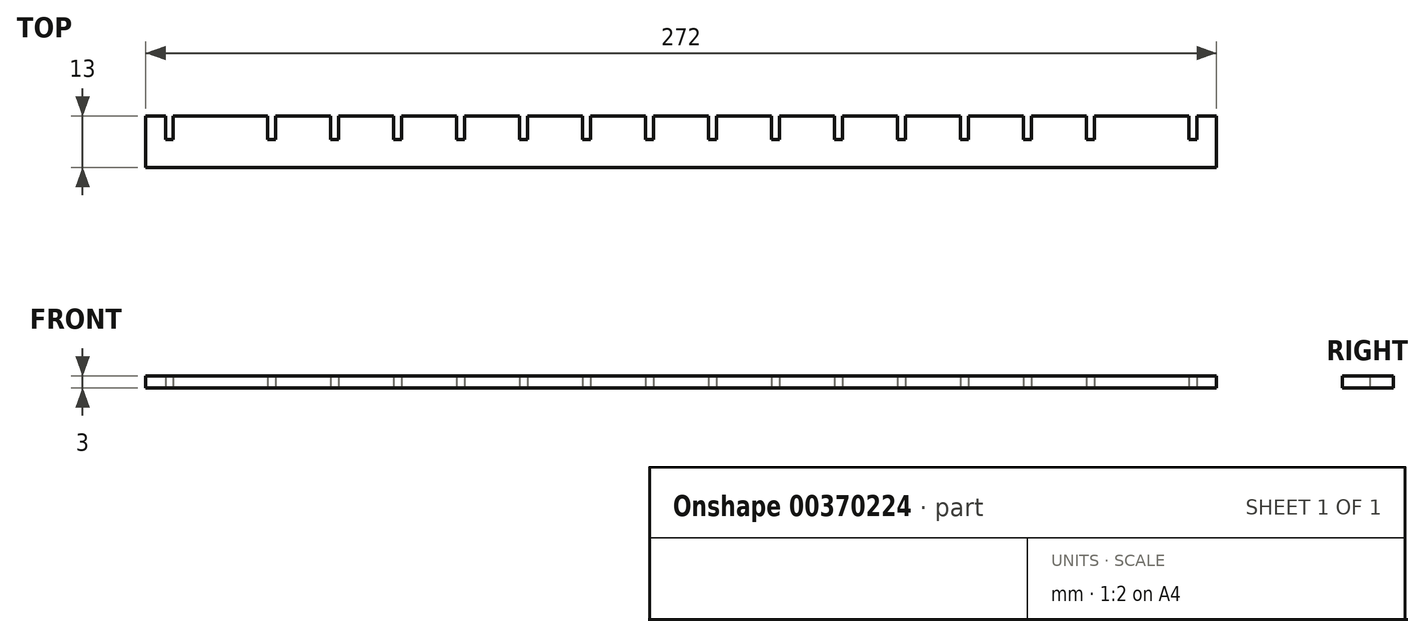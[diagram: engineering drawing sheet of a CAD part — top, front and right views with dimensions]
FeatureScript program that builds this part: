
annotation { "Feature Type Name" : "Feature", "Feature Type Description" : "" }
export const myFeature = defineFeature(function(context is Context, id is Id, definition is map)
    precondition{}
    {
        {
            var Q0;
            Q0=qCreatedBy(makeId("Top.planeOp"),FACE);
            var sketch = newSketch(context, id + "F0", { "sketchPlane" : qUnion([Q0])});
            skLineSegment(sketch, "E0.bottom", {"start": v(-189.77, 23.41) * mm, "end": v(82.23, 23.41) * mm});
            skLineSegment(sketch, "E0.top", {"start": v(-189.77, 10.41) * mm, "end": v(82.23, 10.41) * mm});
            skLineSegment(sketch, "E0.left", {"start": v(-189.77, 23.41) * mm, "end": v(-189.77, 10.41) * mm});
            skLineSegment(sketch, "E0.right", {"start": v(82.23, 23.41) * mm, "end": v(82.23, 10.41) * mm});
            skLineSegment(sketch, "E1.bottom", {"start": v(49.23, 23.41) * mm, "end": v(51.23, 23.41) * mm});
            skLineSegment(sketch, "E1.top", {"start": v(49.23, 17.41) * mm, "end": v(51.23, 17.41) * mm});
            skLineSegment(sketch, "E1.left", {"start": v(49.23, 23.41) * mm, "end": v(49.23, 17.41) * mm});
            skLineSegment(sketch, "E1.right", {"start": v(51.23, 23.41) * mm, "end": v(51.23, 17.41) * mm});
            skLineSegment(sketch, "E2.bottom", {"start": v(35.23, 23.41) * mm, "end": v(33.23, 23.41) * mm});
            skLineSegment(sketch, "E2.top", {"start": v(35.23, 17.41) * mm, "end": v(33.23, 17.41) * mm});
            skLineSegment(sketch, "E2.left", {"start": v(35.23, 23.41) * mm, "end": v(35.23, 17.41) * mm});
            skLineSegment(sketch, "E2.right", {"start": v(33.23, 23.41) * mm, "end": v(33.23, 17.41) * mm});
            skLineSegment(sketch, "E3.bottom", {"start": v(19.23, 23.41) * mm, "end": v(17.23, 23.41) * mm});
            skLineSegment(sketch, "E3.top", {"start": v(19.23, 17.41) * mm, "end": v(17.23, 17.41) * mm});
            skLineSegment(sketch, "E3.left", {"start": v(19.23, 23.41) * mm, "end": v(19.23, 17.41) * mm});
            skLineSegment(sketch, "E3.right", {"start": v(17.23, 23.41) * mm, "end": v(17.23, 17.41) * mm});
            skLineSegment(sketch, "E4.bottom", {"start": v(3.23, 23.41) * mm, "end": v(1.23, 23.41) * mm});
            skLineSegment(sketch, "E4.top", {"start": v(3.23, 17.41) * mm, "end": v(1.23, 17.41) * mm});
            skLineSegment(sketch, "E4.left", {"start": v(3.23, 23.41) * mm, "end": v(3.23, 17.41) * mm});
            skLineSegment(sketch, "E4.right", {"start": v(1.23, 23.41) * mm, "end": v(1.23, 17.41) * mm});
            skLineSegment(sketch, "E5.bottom", {"start": v(-12.77, 23.41) * mm, "end": v(-14.77, 23.41) * mm});
            skLineSegment(sketch, "E5.top", {"start": v(-12.77, 17.41) * mm, "end": v(-14.77, 17.41) * mm});
            skLineSegment(sketch, "E5.left", {"start": v(-12.77, 23.41) * mm, "end": v(-12.77, 17.41) * mm});
            skLineSegment(sketch, "E5.right", {"start": v(-14.77, 23.41) * mm, "end": v(-14.77, 17.41) * mm});
            skLineSegment(sketch, "E6.bottom", {"start": v(-28.77, 23.41) * mm, "end": v(-30.77, 23.41) * mm});
            skLineSegment(sketch, "E6.top", {"start": v(-28.77, 17.41) * mm, "end": v(-30.77, 17.41) * mm});
            skLineSegment(sketch, "E6.left", {"start": v(-28.77, 23.41) * mm, "end": v(-28.77, 17.41) * mm});
            skLineSegment(sketch, "E6.right", {"start": v(-30.77, 23.41) * mm, "end": v(-30.77, 17.41) * mm});
            skLineSegment(sketch, "E7.bottom", {"start": v(-108.77, 23.41) * mm, "end": v(-110.77, 23.41) * mm});
            skLineSegment(sketch, "E7.top", {"start": v(-108.77, 17.41) * mm, "end": v(-110.77, 17.41) * mm});
            skLineSegment(sketch, "E7.left", {"start": v(-108.77, 23.41) * mm, "end": v(-108.77, 17.41) * mm});
            skLineSegment(sketch, "E7.right", {"start": v(-110.77, 23.41) * mm, "end": v(-110.77, 17.41) * mm});
            skLineSegment(sketch, "E8.bottom", {"start": v(-44.77, 23.41) * mm, "end": v(-46.77, 23.41) * mm});
            skLineSegment(sketch, "E8.top", {"start": v(-44.77, 17.41) * mm, "end": v(-46.77, 17.41) * mm});
            skLineSegment(sketch, "E8.left", {"start": v(-44.77, 23.41) * mm, "end": v(-44.77, 17.41) * mm});
            skLineSegment(sketch, "E8.right", {"start": v(-46.77, 23.41) * mm, "end": v(-46.77, 17.41) * mm});
            skLineSegment(sketch, "E9.bottom", {"start": v(-62.77, 23.41) * mm, "end": v(-60.77, 23.41) * mm});
            skLineSegment(sketch, "E9.top", {"start": v(-62.77, 17.41) * mm, "end": v(-60.77, 17.41) * mm});
            skLineSegment(sketch, "E9.left", {"start": v(-62.77, 23.41) * mm, "end": v(-62.77, 17.41) * mm});
            skLineSegment(sketch, "E9.right", {"start": v(-60.77, 23.41) * mm, "end": v(-60.77, 17.41) * mm});
            skLineSegment(sketch, "E10.bottom", {"start": v(-78.77, 23.41) * mm, "end": v(-76.77, 23.41) * mm});
            skLineSegment(sketch, "E10.top", {"start": v(-78.77, 17.41) * mm, "end": v(-76.77, 17.41) * mm});
            skLineSegment(sketch, "E10.left", {"start": v(-78.77, 23.41) * mm, "end": v(-78.77, 17.41) * mm});
            skLineSegment(sketch, "E10.right", {"start": v(-76.77, 23.41) * mm, "end": v(-76.77, 17.41) * mm});
            skLineSegment(sketch, "E11.bottom", {"start": v(-94.77, 23.41) * mm, "end": v(-92.77, 23.41) * mm});
            skLineSegment(sketch, "E11.top", {"start": v(-94.77, 17.41) * mm, "end": v(-92.77, 17.41) * mm});
            skLineSegment(sketch, "E11.left", {"start": v(-94.77, 23.41) * mm, "end": v(-94.77, 17.41) * mm});
            skLineSegment(sketch, "E11.right", {"start": v(-92.77, 23.41) * mm, "end": v(-92.77, 17.41) * mm});
            skLineSegment(sketch, "E12.bottom", {"start": v(-126.77, 23.41) * mm, "end": v(-124.77, 23.41) * mm});
            skLineSegment(sketch, "E12.top", {"start": v(-126.77, 17.41) * mm, "end": v(-124.77, 17.41) * mm});
            skLineSegment(sketch, "E12.left", {"start": v(-126.77, 23.41) * mm, "end": v(-126.77, 17.41) * mm});
            skLineSegment(sketch, "E12.right", {"start": v(-124.77, 23.41) * mm, "end": v(-124.77, 17.41) * mm});
            skLineSegment(sketch, "E13.bottom", {"start": v(-142.77, 23.41) * mm, "end": v(-140.77, 23.41) * mm});
            skLineSegment(sketch, "E13.top", {"start": v(-142.77, 17.41) * mm, "end": v(-140.77, 17.41) * mm});
            skLineSegment(sketch, "E13.left", {"start": v(-142.77, 23.41) * mm, "end": v(-142.77, 17.41) * mm});
            skLineSegment(sketch, "E13.right", {"start": v(-140.77, 23.41) * mm, "end": v(-140.77, 17.41) * mm});
            skLineSegment(sketch, "E14.bottom", {"start": v(-158.77, 23.41) * mm, "end": v(-156.77, 23.41) * mm});
            skLineSegment(sketch, "E14.top", {"start": v(-158.77, 17.41) * mm, "end": v(-156.77, 17.41) * mm});
            skLineSegment(sketch, "E14.left", {"start": v(-158.77, 23.41) * mm, "end": v(-158.77, 17.41) * mm});
            skLineSegment(sketch, "E14.right", {"start": v(-156.77, 23.41) * mm, "end": v(-156.77, 17.41) * mm});
            skLineSegment(sketch, "E15.bottom", {"start": v(75.23, 23.41) * mm, "end": v(77.23, 23.41) * mm});
            skLineSegment(sketch, "E15.top", {"start": v(75.23, 17.41) * mm, "end": v(77.23, 17.41) * mm});
            skLineSegment(sketch, "E15.left", {"start": v(75.23, 23.41) * mm, "end": v(75.23, 17.41) * mm});
            skLineSegment(sketch, "E15.right", {"start": v(77.23, 23.41) * mm, "end": v(77.23, 17.41) * mm});
            skLineSegment(sketch, "E16.bottom", {"start": v(-184.77, 23.41) * mm, "end": v(-182.77, 23.41) * mm});
            skLineSegment(sketch, "E16.top", {"start": v(-184.77, 17.41) * mm, "end": v(-182.77, 17.41) * mm});
            skLineSegment(sketch, "E16.left", {"start": v(-184.77, 23.41) * mm, "end": v(-184.77, 17.41) * mm});
            skLineSegment(sketch, "E16.right", {"start": v(-182.77, 23.41) * mm, "end": v(-182.77, 17.41) * mm});
            skSolve(sketch);
        }
        {
            var Q0;
            Q0=makeQuery(id+"F0.imprint","IMPRINT",FACE,{"disambiguationData":[TD([[makeQuery(id+"F0.imprint","IMPRINT",EDGE,{"derivedFrom":sQuery(id+"F0.wireOp",EDGE,"E0.top")}),1.0]])]});
            extrude(context, id + "F1", {"entities" : qUnion([Q0]), "depth" : 3 * mm});
        }
    });
